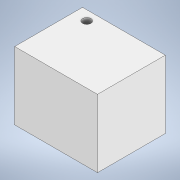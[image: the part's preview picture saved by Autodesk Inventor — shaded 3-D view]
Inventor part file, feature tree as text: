
AUTODESK INVENTOR PART (.ipt)
format: ipt  version: 2022 (Build 260153000, 153)  size: 96,256 bytes
history: native  units: in
note: dims shown in document units (in); Inventor stores cm internally (conversion verified against a paired STEP export)
features: extrude x2, sketch x2
ambient origin geometry x8: Origin, YZ Plane, XZ Plane, XY Plane, X Axis, Y Axis, Z Axis, Center Point
bodies: Solid1 (feature_tree)
feature tree (4):
  extrude  "Extrusion1"  Depth=17.0in
  extrude  "Extrusion2"  Depth=17.0in
  sketch  "Sketch1"  dims[d0=20.75in d1=17.0in]
  sketch  "Sketch2"  dims[d2=17.0in d3=0.0in d4=2.1in d5=17.0in d6=0.0in]
